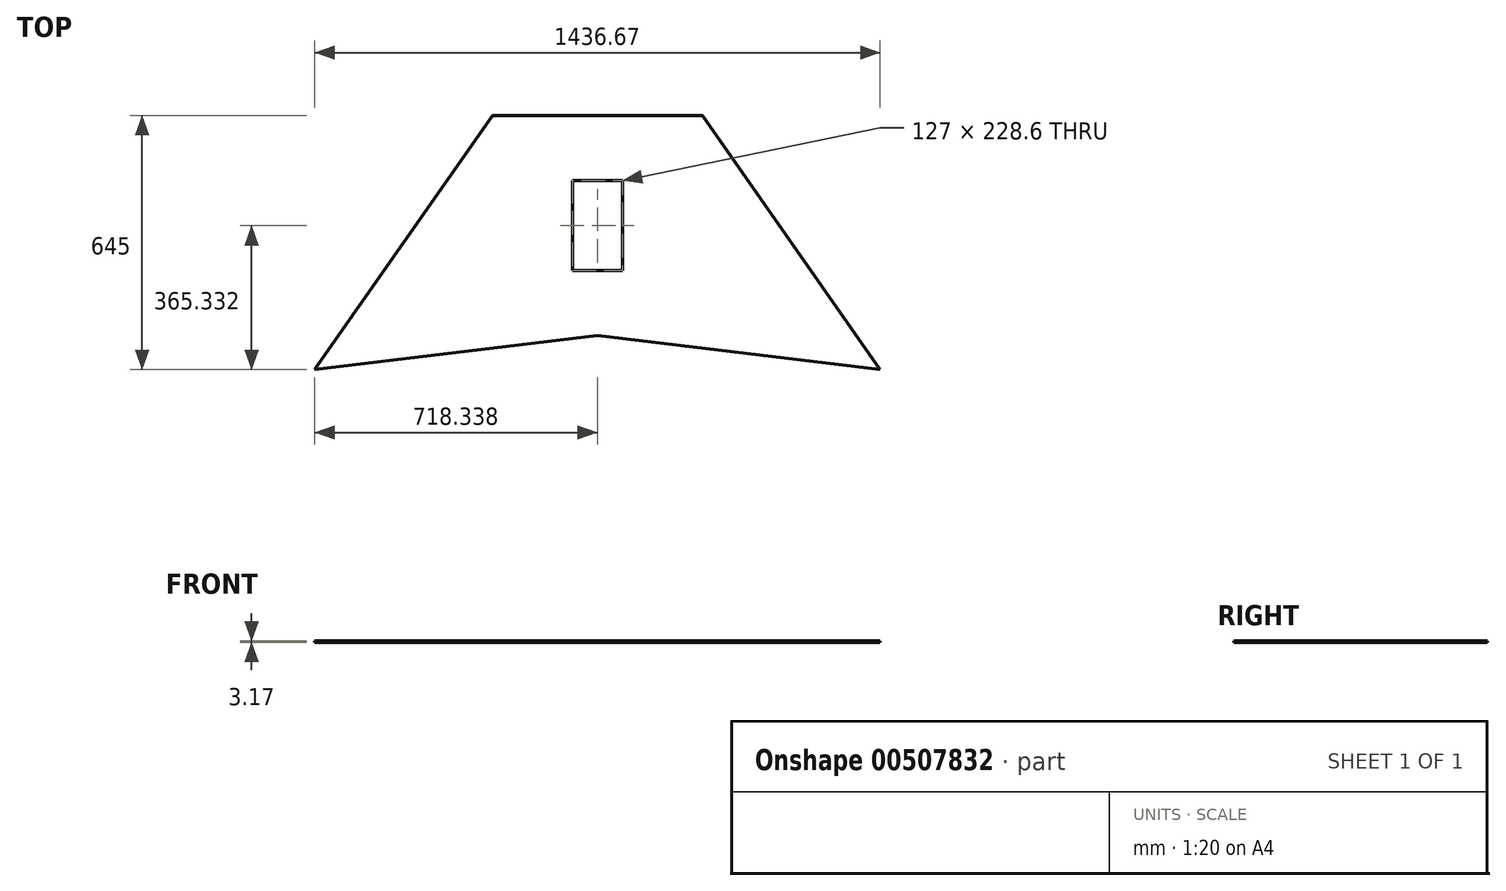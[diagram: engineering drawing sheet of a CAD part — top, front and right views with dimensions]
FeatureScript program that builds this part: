
annotation { "Feature Type Name" : "Feature", "Feature Type Description" : "" }
export const myFeature = defineFeature(function(context is Context, id is Id, definition is map)
    precondition{}
    {
        {
            var Q0;
            Q0=qCreatedBy(makeId("Top.planeOp"),FACE);
            var sketch = newSketch(context, id + "F0", { "sketchPlane" : qUnion([Q0])});
            skLineSegment(sketch, "E0", {"start": v(-38.7, 342.9) * mm, "end": v(494.7, 342.9) * mm});
            skLineSegment(sketch, "E1", {"start": v(-38.7, 342.9) * mm, "end": v(-490.33, -302.1) * mm});
            skLineSegment(sketch, "E2", {"start": v(494.7, 342.9) * mm, "end": v(946.34, -302.1) * mm});
            skLineSegment(sketch, "E3", {"start": v(228, -216.43) * mm, "end": v(228, 342.9) * mm, "construction": true});
            skLineSegment(sketch, "E4.bottom", {"start": v(164.5, 177.53) * mm, "end": v(291.5, 177.53) * mm});
            skLineSegment(sketch, "E4.top", {"start": v(164.5, -51.07) * mm, "end": v(291.5, -51.07) * mm});
            skLineSegment(sketch, "E4.left", {"start": v(164.5, 177.53) * mm, "end": v(164.5, -51.07) * mm});
            skLineSegment(sketch, "E4.right", {"start": v(291.5, 177.53) * mm, "end": v(291.5, -51.07) * mm});
            skPoint(sketch, "E4.middle", {"position": v(228, 63.23) * mm});
            skLineSegment(sketch, "E5", {"start": v(-490.33, -302.1) * mm, "end": v(228, -216.43) * mm});
            skLineSegment(sketch, "E6", {"start": v(228, -216.43) * mm, "end": v(946.34, -302.1) * mm});
            skSolve(sketch);
        }
        {
            var Q0;
            Q0=makeQuery(id+"F0.imprint","IMPRINT",FACE,{"disambiguationData":[TD([[makeQuery(id+"F0.imprint","IMPRINT",EDGE,{"derivedFrom":sQuery(id+"F0.wireOp",EDGE,"E0")}),-1.0]])]});
            extrude(context, id + "F1", {"entities" : qUnion([Q0]), "depth" : 3.17 * mm, "offsetDistance" : 25.4 * mm});
        }
    });
